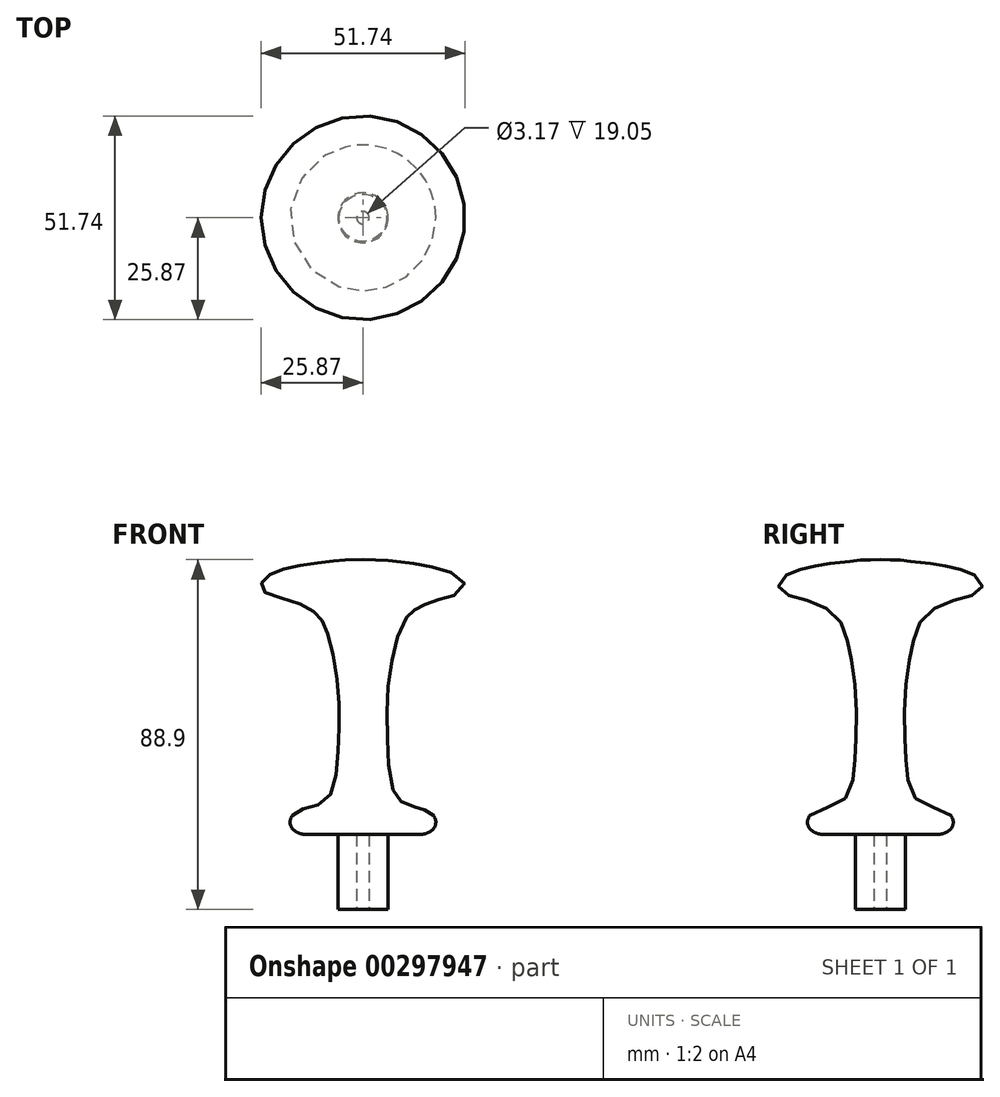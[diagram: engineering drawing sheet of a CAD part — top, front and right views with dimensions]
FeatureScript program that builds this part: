
annotation { "Feature Type Name" : "Feature", "Feature Type Description" : "" }
export const myFeature = defineFeature(function(context is Context, id is Id, definition is map)
    precondition{}
    {
        {
            var Q0;
            Q0=qCreatedBy(makeId("Front.planeOp"),FACE);
            var sketch = newSketch(context, id + "F0", { "sketchPlane" : qUnion([Q0])});
            skLineSegment(sketch, "E0", {"start": v(0, 0) * mm, "end": v(-6.35, 0) * mm});
            skLineSegment(sketch, "E1", {"start": v(-6.35, 0) * mm, "end": v(-6.35, 19.05) * mm});
            skLineSegment(sketch, "E2", {"start": v(-6.35, 19.05) * mm, "end": v(-19.05, 19.05) * mm});
            skLineSegment(sketch, "E3", {"start": v(-19.05, 19.05) * mm, "end": v(-19.05, 22.23) * mm});
            skLineSegment(sketch, "E4", {"start": v(0, 0) * mm, "end": v(0, 88.9) * mm, "construction": true});
            skLineSegment(sketch, "E5", {"start": v(7.26, 0) * mm, "end": v(7.26, 63.5) * mm, "construction": true});
            skLineSegment(sketch, "E6", {"start": v(3.2, 0) * mm, "end": v(4.85, 101.59) * mm, "construction": true});
            skLineSegment(sketch, "E7", {"start": v(-6.35, 19.05) * mm, "end": v(-6.35, 88.65) * mm, "construction": true});
            skPoint(sketch, "E8.2.internal.snap0", {"position": v(-12.7, 19.05) * mm});
            skFitSpline(sketch, "E9", {"points": [v(-19.05, 22.23) * mm, v(-15.28, 25.51) * mm, v(-9, 28.15) * mm, v(-6.35, 40.34) * mm, v(-6.35, 56.12) * mm, v(-9.2, 70.84) * mm, v(-11.52, 74.8) * mm, v(-17.31, 78.12) * mm, v(-25.4, 81.06) * mm, v(-25.4, 83.6) * mm, v(-20.98, 86.2) * mm, v(-13.36, 87.8) * mm, v(-6.35, 88.65) * mm, v(0, 88.9) * mm], "startDerivative": vector(58.39, 97.21) * mm, "endDerivative": vector(163.16, 0.36) * mm});
            skPoint(sketch, "E10", {"position": v(-6.35, 53.85) * mm});
            skLineSegment(sketch, "E11", {"start": v(0, 0) * mm, "end": v(0, 88.9) * mm});
            skLineSegment(sketch, "E12", {"start": v(-25.4, 83.6) * mm, "end": v(0, 83.6) * mm, "construction": true});
            skLineSegment(sketch, "E13", {"start": v(-25.4, 81.06) * mm, "end": v(0, 81.06) * mm, "construction": true});
            skSolve(sketch);
        }
        {
            var Q0;
            Q0=makeQuery(id+"F0.imprint","IMPRINT",FACE,{"disambiguationData":[TD([[makeQuery(id+"F0.imprint","IMPRINT",EDGE,{"derivedFrom":sQuery(id+"F0.wireOp",EDGE,"E0")}),-1.0]])]});
            var Q1;
            Q1=sQuery(id+"F0.wireOp",EDGE,"E11");
            revolve(context, id + "F1", {"entities" : qUnion([Q0]), "axis" : qUnion([Q1]), "revolveType" : RevolveType.FULL});
        }
        {
            var Q0;
            Q0=makeQuery(id+"F1.opRevolve","SWEPT_EDGE",EDGE,{"disambiguationData":[OSD([sQuery(id+"F0.wireOp",EDGE,"E2"),sQuery(id+"F0.wireOp",EDGE,"E3")])]});
            fillet(context, id + "F2", {"entities" : qUnion([Q0]), "radius" : 5.08 * mm, "tangentPropagation" : true, "allowEdgeOverflow" : false});
        }
        {
            var Q0;
            Q0=makeQuery(id+"F1.opRevolve","SWEPT_FACE",FACE,{"disambiguationData":[OSD([sQuery(id+"F0.wireOp",EDGE,"E0")])]});
            var sketch = newSketch(context, id + "F3", { "sketchPlane" : qUnion([Q0])});
            skPoint(sketch, "E14", {"position": v(0, 0) * mm});
            skSolve(sketch);
        }
        {
            var Q0;
            Q0=makeQuery(id+"F3.imprint","IMPRINT",FACE,{"disambiguationData":[TD([[makeQuery(id+"F3.imprint","IMPRINT",EDGE,{"derivedFrom":makeQuery(id+"F1.opRevolve","SWEPT_EDGE",EDGE,{"disambiguationData":[OSD([sQuery(id+"F0.wireOp",EDGE,"E0"),sQuery(id+"F0.wireOp",EDGE,"E1")])]})}),1.0]])]});
            var sketch = newSketch(context, id + "F4", { "sketchPlane" : qUnion([Q0])});
            skCircle(sketch, "E15", {"center": v(0, 0) * mm, "radius": 1.59 * mm});
            skSolve(sketch);
        }
        {
            var Q0;
            Q0 = qSketchRegion(id + "F4", true);
            extrude(context, id + "F5", {"entities" : qUnion([Q0]), "operationType" : NewBodyOperationType.REMOVE, "oppositeDirection" : true, "depth" : 19.05 * mm});
        }
        {
            var Q0;
            Q0=makeQuery(id+"F2.opFillet","BLEND_EDGE",EDGE,{"blendedFrom":[makeQuery(id+"F1.opRevolve","SWEPT_EDGE",EDGE,{"disambiguationData":[OSD([sQuery(id+"F0.wireOp",EDGE,"E2"),sQuery(id+"F0.wireOp",EDGE,"E3")])]}),makeQuery(id+"F1.opRevolve","SWEPT_FACE",FACE,{"disambiguationData":[OSD([sQuery(id+"F0.wireOp",EDGE,"E9")])]})],"blendedInto":[makeQuery(id+"F1.opRevolve","SWEPT_FACE",FACE,{"disambiguationData":[OSD([sQuery(id+"F0.wireOp",EDGE,"E9")])]})]});
            fillet(context, id + "F6", {"entities" : qUnion([Q0]), "radius" : 2.54 * mm, "tangentPropagation" : true, "allowEdgeOverflow" : false});
        }
    });
